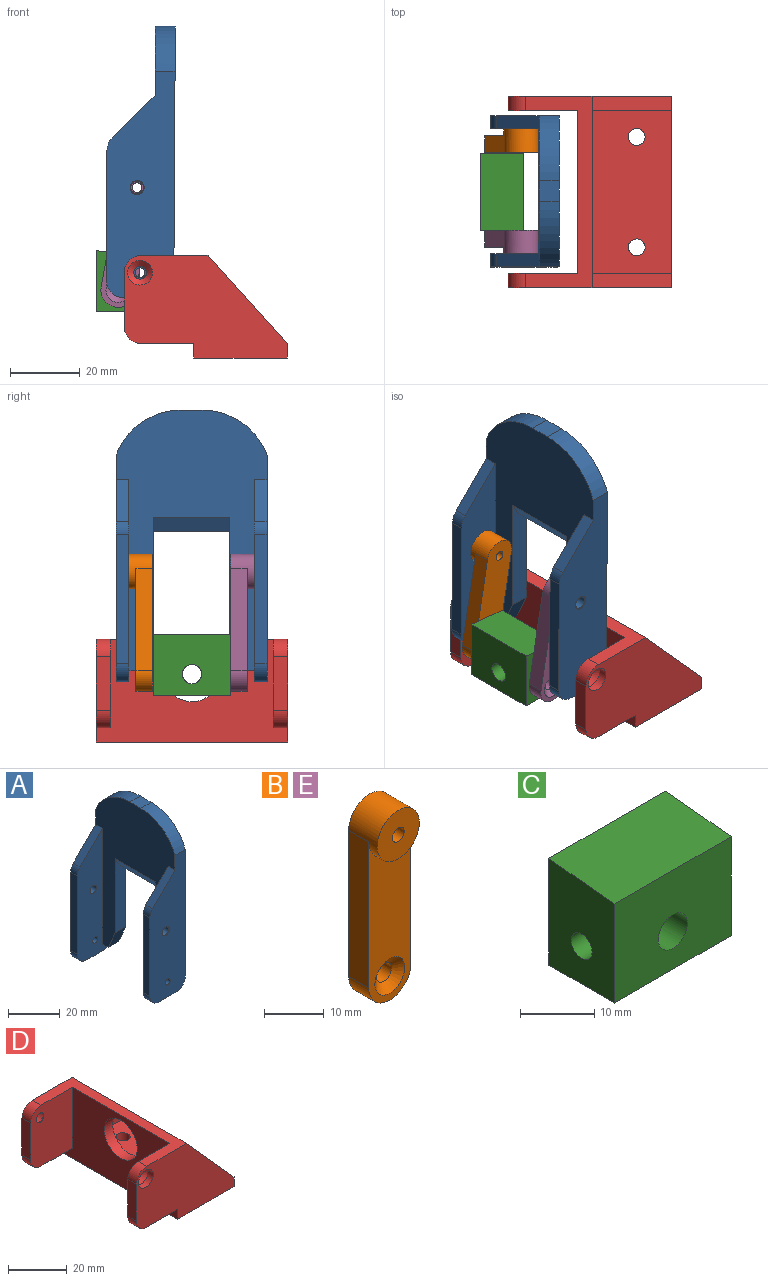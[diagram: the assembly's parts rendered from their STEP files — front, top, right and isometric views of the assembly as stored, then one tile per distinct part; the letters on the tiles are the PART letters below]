
ASSEMBLY  parts=5 mates=6
PART A: 35 faces, bbox 19.5x43.5x78.2 mm
  f0: plane 75x43.46mm, normal (-1,0,0), area 1714.5mm2, adj f4,f5,f13,f14,f20,f21,f24,f25
  f1: plane 73.1x43.46mm, normal (1,0,0), area 2184.9mm2, adj f4,f8,f13,f17,f20,f26,f28,f29
  f2: cone r=3.54mm half-angle=50deg, axis (0,-1,0), area 3.2mm2, adj f23,f34
  f3: cylinder r=1.4mm len=3.73mm, axis (0,-1,0), area 32.7mm2, adj f27,f34
  f4: cylinder r=20mm len=18.73mm, axis (-1,0,0), area 138.6mm2, adj f0,f1,f26,f34
  f5: plane 12.24x12.24mm, normal (-0.71,0,0.71), area 64.6mm2, adj f0,f9,f27,f34
  f6: plane 37.26x3.73mm, normal (-1,0,0), area 139mm2, adj f9,f10,f27,f34
  f7: plane 9.29x3.73mm, normal (0,0,-1), area 34.6mm2, adj f8,f10,f27,f34
  f8: cylinder r=5.08mm len=7.74mm, axis (0,1,0), area 36.8mm2, adj f1,f7,f24,f27,f32,f34
  f9: cylinder r=5.08mm len=3.73mm, axis (0,-1,0), area 14.9mm2, adj f5,f6,f27,f34
  f10: cylinder r=5.08mm len=5.08mm, axis (0,-1,0), area 29.8mm2, adj f6,f7,f27,f34
  f11: cone r=3.54mm half-angle=50deg, axis (0,1,0), area 3.2mm2, adj f22,f33
  f12: cylinder r=1.4mm len=3.73mm, axis (0,1,0), area 32.7mm2, adj f25,f33
  f13: cylinder r=20mm len=18.73mm, axis (1,0,0), area 138.6mm2, adj f0,f1,f26,f33
  f14: plane 12.24x12.24mm, normal (-0.71,0,0.71), area 64.6mm2, adj f0,f19,f25,f33
  f15: plane 37.26x3.73mm, normal (-1,0,0), area 139mm2, adj f18,f19,f25,f33
  f16: plane 9.29x3.73mm, normal (0,0,-1), area 34.6mm2, adj f17,f18,f25,f33
  f17: cylinder r=5.08mm len=7.74mm, axis (0,-1,0), area 36.8mm2, adj f1,f16,f21,f25,f31,f33
  f18: cylinder r=5.08mm len=5.08mm, axis (0,1,0), area 29.8mm2, adj f15,f16,f25,f33
  f19: cylinder r=5.08mm len=3.73mm, axis (0,1,0), area 14.9mm2, adj f14,f15,f25,f33
  f20: plane 35.11x5.72mm, normal (0,1,0), area 182.4mm2, adj f0,f1,f28,f30,f32
  f21: plane 5.34x3.19mm, normal (0,0,-1), area 17mm2, adj f0,f17,f25,f31
  f22: cylinder r=1.83mm len=3.66mm, axis (0,1,0), area 40.9mm2, adj f11,f25
  f23: cylinder r=1.83mm len=3.66mm, axis (0,-1,0), area 40.9mm2, adj f2,f27
  f24: plane 5.34x3.19mm, normal (0,0,-1), area 17mm2, adj f0,f8,f27,f32
  f25: plane 58.18x19.08mm, normal (0,-1,0), area 694.6mm2, adj f0,f12,f14,f15,f16,f17,f18,f19
  f26: plane 6x5.72mm, normal (0,0,1), area 34.3mm2, adj f0,f1,f4,f13
  f27: plane 58.18x19.08mm, normal (0,1,0), area 694.6mm2, adj f0,f3,f5,f6,f7,f8,f9,f10
  f28: plane 22x3.41mm, normal (0,0,-1), area 74.9mm2, adj f1,f20,f29,f30
  f29: plane 35.11x5.72mm, normal (0,-1,0), area 182.4mm2, adj f0,f1,f28,f30,f31
  f30: plane 22x4mm, normal (-0.87,0,-0.5), area 101.6mm2, adj f0,f20,f28,f29
  f31: plane 8.91x5.73mm, normal (0,-0.92,-0.39), area 55mm2, adj f0,f1,f17,f21,f29
  f32: plane 8.91x5.73mm, normal (0,0.92,-0.39), area 55mm2, adj f0,f1,f8,f20,f24
  f33: plane 65.19x19.45mm, normal (0,1,0), area 1046.4mm2, adj f0,f1,f11,f12,f13,f14,f15,f16
  f34: plane 65.19x19.45mm, normal (0,-1,0), area 1046.4mm2, adj f0,f1,f2,f3,f4,f5,f6,f7
PART B: 10 faces, bbox 10x6.8x40 mm
  f0: cone r=3.54mm half-angle=50deg, axis (0,-1,0), area 37.8mm2, adj f1,f4
  f1: cylinder r=1.83mm len=3.66mm, axis (0,-1,0), area 38.2mm2, adj f0,f9
  f2: cylinder r=1.4mm len=6.76mm, axis (0,1,0), area 59.4mm2, adj f8,f9
  f3: cylinder r=5mm len=10mm, axis (0,1,0), area 137.6mm2, adj f4,f6,f7,f8,f9
  f4: plane 35x10mm, normal (0,-1,0), area 260.6mm2, adj f0,f3,f5,f6,f7
  f5: cylinder r=5mm len=10mm, axis (0,1,0), area 74.8mm2, adj f4,f6,f7,f9
  f6: plane 30x4.76mm, normal (1,0,0), area 142.9mm2, adj f3,f4,f5,f9
  f7: plane 30x4.76mm, normal (-1,0,0), area 142.9mm2, adj f3,f4,f5,f9
  f8: plane 10x10mm, normal (0,-1,0), area 72.4mm2, adj f2,f3
  f9: plane 40x10mm, normal (0,1,0), area 361.9mm2, adj f1,f2,f3,f5,f6,f7
PART C: 9 faces, bbox 22.2x12.5x17.6 mm
  f0: plane 22.23x16.31mm, normal (0,-1,0), area 338.2mm2, adj f2,f4,f5,f7,f8
  f1: plane 22.23x17.58mm, normal (0,1,0), area 366.5mm2, adj f2,f4,f5,f7,f8
  f2: plane 22.23x12.5mm, normal (0,0,-1), area 277.8mm2, adj f0,f1,f7,f8
  f3: cylinder r=1.98mm len=9.17mm, axis (1,0,0), area 108.9mm2, adj f5,f8
  f4: plane 22.23x12.5mm, normal (0,-0.1,0.99), area 279.2mm2, adj f0,f1,f7,f8
  f5: cylinder r=2.78mm len=12.5mm, axis (0,-1,0), area 191.5mm2, adj f0,f1,f3,f6
  f6: cylinder r=1.98mm len=9.17mm, axis (1,0,0), area 108.9mm2, adj f5,f7
  f7: plane 17.58x12.5mm, normal (1,0,0), area 199.4mm2, adj f0,f1,f2,f4,f6
  f8: plane 17.58x12.5mm, normal (-1,0,0), area 199.4mm2, adj f0,f1,f2,f3,f4
PART D: 31 faces, bbox 47x55.1x29.5 mm
  f0: plane 46.83x22.86mm, normal (0,0,1), area 1033.8mm2, adj f1,f7,f8,f10,f25,f27
  f1: plane 46.83x25.4mm, normal (1,0,0), area 991.4mm2, adj f0,f6,f11,f25,f27
  f2: cone r=3.54mm half-angle=50deg, axis (0,1,0), area 37.8mm2, adj f3,f29
  f3: cylinder r=1.83mm len=3.66mm, axis (0,1,0), area 1.7mm2, adj f2,f13
  f4: cone r=3.54mm half-angle=50deg, axis (0,-1,0), area 37.8mm2, adj f5,f22
  f5: cylinder r=1.83mm len=3.66mm, axis (0,-1,0), area 1.7mm2, adj f4,f15
  f6: cylinder r=7.94mm len=15.88mm, axis (-1,0,0), area 205.8mm2, adj f1,f9
  f7: cylinder r=2.41mm len=4.83mm, axis (0,0,1), area 62.6mm2, adj f0,f24
  f8: cylinder r=2.41mm len=4.83mm, axis (0,0,1), area 62.6mm2, adj f0,f24
  f9: plane 55.08x29.53mm, normal (-1,0,0), area 1218.8mm2, adj f6,f11,f12,f13,f15,f16,f23,f24
  f10: plane 55.08x4.13mm, normal (1,0,0), area 227.3mm2, adj f0,f23,f24,f26,f28,f30
  f11: plane 55.08x19.13mm, normal (0,0,1), area 351.2mm2, adj f1,f9,f13,f15,f20,f21,f23,f26
  f12: plane 15x4.13mm, normal (0,0,-1), area 61.9mm2, adj f9,f13,f19,f30
  f13: plane 25.4x20mm, normal (0,-1,0), area 486.8mm2, adj f3,f9,f11,f12,f14,f19,f20
  f14: plane 15.4x4.13mm, normal (-1,0,0), area 63.6mm2, adj f13,f19,f20,f30
  f15: plane 25.4x20mm, normal (0,1,0), area 486.8mm2, adj f5,f9,f11,f16,f17,f18,f21
  f16: plane 15x4.13mm, normal (0,0,-1), area 61.9mm2, adj f9,f15,f18,f23
  f17: plane 15.4x4.13mm, normal (-1,0,0), area 63.6mm2, adj f15,f18,f21,f23
  f18: cylinder r=5mm len=5mm, axis (0,-1,0), area 32.4mm2, adj f15,f16,f17,f23
  f19: cylinder r=5mm len=5mm, axis (0,1,0), area 32.4mm2, adj f12,f13,f14,f30
  f20: cylinder r=5mm len=5mm, axis (0,-1,0), area 32.4mm2, adj f11,f13,f14,f30
  f21: cylinder r=5mm len=5mm, axis (0,1,0), area 32.4mm2, adj f11,f15,f17,f23
  f22: cylinder r=3.54mm len=7.09mm, axis (0,1,0), area 56.5mm2, adj f4,f23
  f23: plane 46.99x29.53mm, normal (0,-1,0), area 964.4mm2, adj f9,f10,f11,f16,f17,f18,f21,f22
  f24: plane 55.08x26.99mm, normal (0,0,-1), area 1449.9mm2, adj f7,f8,f9,f10,f23,f30
  f25: plane 25.4x22.86mm, normal (0,1,0), area 290.3mm2, adj f0,f1,f26
  f26: plane 25.4x22.86mm, normal (0.74,0,0.67), area 141mm2, adj f10,f11,f23,f25
  f27: plane 25.4x22.86mm, normal (0,-1,0), area 290.3mm2, adj f0,f1,f28
  f28: plane 25.4x22.86mm, normal (0.74,0,0.67), area 141mm2, adj f10,f11,f27,f30
  f29: cylinder r=3.54mm len=7.09mm, axis (0,-1,0), area 56.5mm2, adj f2,f30
  f30: plane 46.99x29.53mm, normal (0,1,0), area 964.4mm2, adj f9,f10,f11,f12,f14,f19,f20,f24
PART E: same geometry as B
PLACE A rot(axis=(0,1,0),0.3deg) t=(4.87,-1.88,-0.12)mm
PLACE B rot(axis=(0.09,0,1),180deg) t=(-21.69,-12.05,16.99)mm
PLACE C rot(axis=(0,0,1),90deg) t=(-27.94,-25,16.99)mm
PLACE D at identity fixed
PLACE E rot(axis=(0,1,0),10.4deg) t=(-21.69,-37.7,16.99)mm
MATE slider C.f5 <-> D.f6  axis (-1,0,0) through (-27.94,-25,16.99)mm
MATE revolute B.f2 <-> A.f2  axis (0,1,0) through (-16.27,-6.88,46.49)mm
MATE revolute C.f3 <-> E.f0  axis (0,-1,0) through (-21.69,-36.11,16.99)mm
MATE revolute E.f2 <-> A.f2  axis (0,-1,0) through (-16.27,-42.88,46.49)mm
MATE cylindrical C.f3 <-> B.f0  axis (0,1,0) through (-21.69,-13.89,16.99)mm
MATE cylindrical A.f3 <-> D.f2  axis (0,-1,0) through (-15.41,-46.61,21.99)mm
